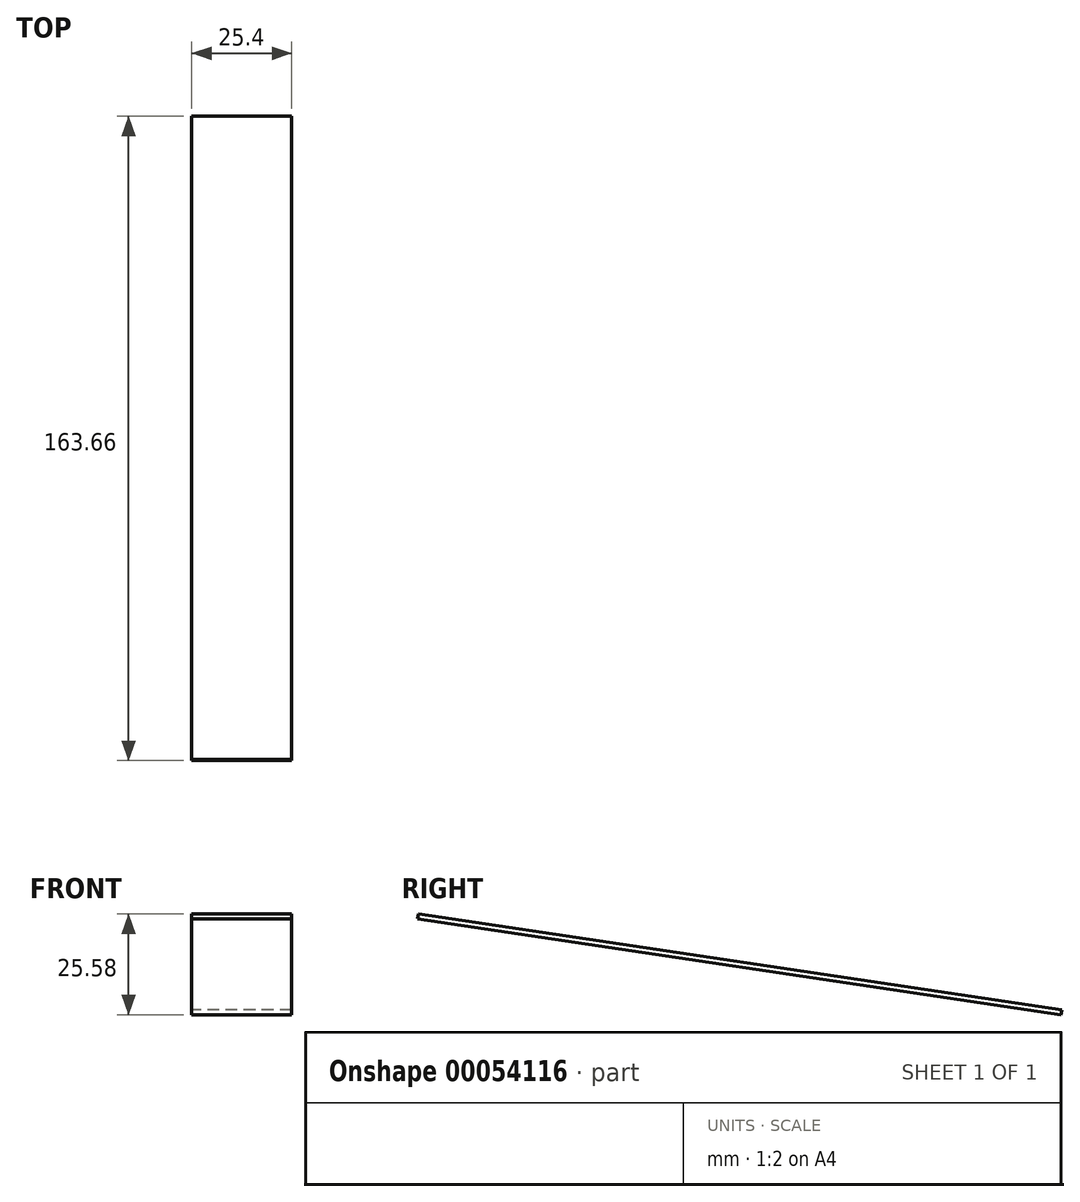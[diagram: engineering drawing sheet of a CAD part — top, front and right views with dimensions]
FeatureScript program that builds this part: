
annotation { "Feature Type Name" : "Feature", "Feature Type Description" : "" }
export const myFeature = defineFeature(function(context is Context, id is Id, definition is map)
    precondition{}
    {
        {
            var Q0;
            Q0=qCreatedBy(makeId("Right.planeOp"),FACE);
            var sketch = newSketch(context, id + "F0", { "sketchPlane" : qUnion([Q0])});
            skLineSegment(sketch, "E0", {"start": v(-82.57, 44.22) * mm, "end": v(80.85, 19.84) * mm});
            skLineSegment(sketch, "E1", {"start": v(80.85, 19.84) * mm, "end": v(80.67, 18.64) * mm});
            skLineSegment(sketch, "E2", {"start": v(80.67, 18.64) * mm, "end": v(-82.81, 43.02) * mm});
            skLineSegment(sketch, "E3", {"start": v(-82.81, 43.02) * mm, "end": v(-82.57, 44.22) * mm});
            skSolve(sketch);
        }
        {
            var Q0;
            Q0=makeQuery(id+"F0.imprint","IMPRINT",FACE,{"disambiguationData":[TD([[makeQuery(id+"F0.imprint","IMPRINT",EDGE,{"derivedFrom":sQuery(id+"F0.wireOp",EDGE,"E0")}),-1.0]])]});
            extrude(context, id + "F1", {"entities" : qUnion([Q0]), "depth" : 25.4 * mm});
        }
    });
